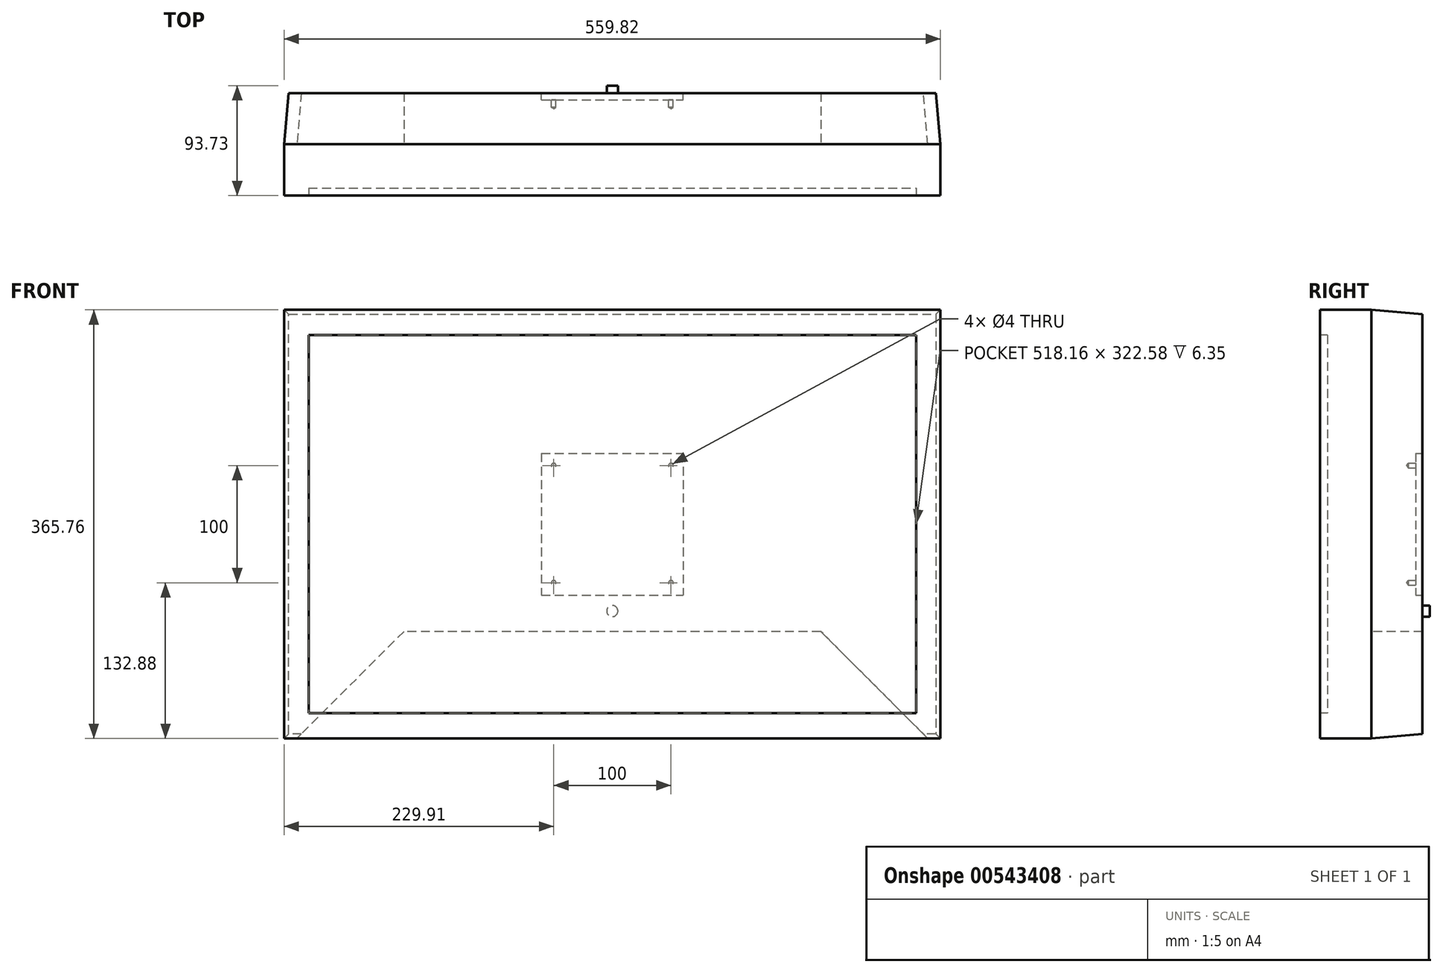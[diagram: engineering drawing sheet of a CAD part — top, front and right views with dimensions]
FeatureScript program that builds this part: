
annotation { "Feature Type Name" : "Feature", "Feature Type Description" : "" }
export const myFeature = defineFeature(function(context is Context, id is Id, definition is map)
    precondition{}
    {
        {
            var Q0;
            Q0=qCreatedBy(makeId("Front.planeOp"),FACE);
            var sketch = newSketch(context, id + "F0", { "sketchPlane" : qUnion([Q0])});
            skLineSegment(sketch, "E0.bottom", {"start": v(-279.9, 182.88) * mm, "end": v(279.9, 182.88) * mm});
            skLineSegment(sketch, "E0.top", {"start": v(-279.9, -182.88) * mm, "end": v(279.9, -182.88) * mm});
            skLineSegment(sketch, "E0.left", {"start": v(-279.9, 182.88) * mm, "end": v(-279.9, -182.88) * mm});
            skLineSegment(sketch, "E0.right", {"start": v(279.9, 182.88) * mm, "end": v(279.9, -182.88) * mm});
            skPoint(sketch, "E0.middle", {"position": v(0, 0) * mm});
            skSolve(sketch);
        }
        {
            var Q0;
            Q0 = qSketchRegion(id + "F0", true);
            extrude(context, id + "F1", {"entities" : qUnion([Q0]), "endBound" : BoundingType.SYMMETRIC, "depth" : 87.38 * mm, "offsetDistance" : 25.4 * mm});
        }
        {
            var Q0;
            Q0=makeQuery(id+"F1.opExtrude","CAP_FACE",FACE,{"disambiguationData":[OSD([sQuery(id+"F0.wireOp",EDGE,"E0.bottom"),sQuery(id+"F0.wireOp",EDGE,"E0.top"),sQuery(id+"F0.wireOp",EDGE,"E0.left"),sQuery(id+"F0.wireOp",EDGE,"E0.right")])],"isStart":false});
            var sketch = newSketch(context, id + "F2", { "sketchPlane" : qUnion([Q0])});
            skLineSegment(sketch, "E1.bottom", {"start": v(-259.08, 161.3) * mm, "end": v(259.08, 161.3) * mm});
            skLineSegment(sketch, "E1.top", {"start": v(-259.08, -161.3) * mm, "end": v(259.08, -161.3) * mm});
            skLineSegment(sketch, "E1.left", {"start": v(-259.08, 161.3) * mm, "end": v(-259.08, -161.3) * mm});
            skLineSegment(sketch, "E1.right", {"start": v(259.08, 161.3) * mm, "end": v(259.08, -161.3) * mm});
            skPoint(sketch, "E1.middle", {"position": v(0, 0) * mm});
            skLineSegment(sketch, "E2", {"start": v(-259.08, -161.3) * mm, "end": v(259.08, 161.3) * mm, "construction": true});
            skSolve(sketch);
        }
        {
            var Q0;
            Q0 = qSketchRegion(id + "F2", true);
            extrude(context, id + "F3", {"entities" : qUnion([Q0]), "operationType" : NewBodyOperationType.REMOVE, "oppositeDirection" : true, "depth" : 6.35 * mm, "offsetDistance" : 25.4 * mm});
        }
        {
            var Q0;
            Q0=makeQuery(id+"F1.opExtrude","CAP_EDGE",EDGE,{"disambiguationData":[OSD([sQuery(id+"F0.wireOp",EDGE,"E0.right")])],"isStart":true});
            var Q1;
            Q1=makeQuery(id+"F1.opExtrude","CAP_EDGE",EDGE,{"disambiguationData":[OSD([sQuery(id+"F0.wireOp",EDGE,"E0.bottom")])],"isStart":true});
            var Q2;
            Q2=makeQuery(id+"F1.opExtrude","CAP_EDGE",EDGE,{"disambiguationData":[OSD([sQuery(id+"F0.wireOp",EDGE,"E0.left")])],"isStart":true});
            var Q3;
            Q3=makeQuery(id+"F1.opExtrude","CAP_EDGE",EDGE,{"disambiguationData":[OSD([sQuery(id+"F0.wireOp",EDGE,"E0.top")])],"isStart":true});
            chamfer(context, id + "F4", {"entities" : qUnion([Q0, Q1, Q2, Q3]), "chamferType" : ChamferType.TWO_OFFSETS, "width1" : ((22.04 - 14.25) / 2) * mm, "oppositeDirection" : false, "width2" : 43.69 * mm, "tangentPropagation" : true});
        }
        {
            var Q0;
            Q0=makeQuery(id+"F1.opExtrude","CAP_FACE",FACE,{"disambiguationData":[OSD([sQuery(id+"F0.wireOp",EDGE,"E0.bottom"),sQuery(id+"F0.wireOp",EDGE,"E0.top"),sQuery(id+"F0.wireOp",EDGE,"E0.left"),sQuery(id+"F0.wireOp",EDGE,"E0.right")])],"isStart":true});
            var sketch = newSketch(context, id + "F5", { "sketchPlane" : qUnion([Q0])});
            skLineSegment(sketch, "E3.bottom", {"start": v(60.45, 60.45) * mm, "end": v(-60.45, 60.45) * mm});
            skLineSegment(sketch, "E3.top", {"start": v(60.45, -60.45) * mm, "end": v(-60.45, -60.45) * mm});
            skLineSegment(sketch, "E3.left", {"start": v(60.45, 60.45) * mm, "end": v(60.45, -60.45) * mm});
            skLineSegment(sketch, "E3.right", {"start": v(-60.45, 60.45) * mm, "end": v(-60.45, -60.45) * mm});
            skPoint(sketch, "E3.middle", {"position": v(0, 0) * mm});
            skSolve(sketch);
        }
        {
            var Q0;
            Q0 = qSketchRegion(id + "F5", true);
            extrude(context, id + "F6", {"entities" : qUnion([Q0]), "operationType" : NewBodyOperationType.REMOVE, "oppositeDirection" : true, "depth" : 5.92 * mm, "offsetDistance" : 25.4 * mm});
        }
        {
            var Q0;
            {var subQ0=sQuery(id+"F0.wireOp",EDGE,"E0.right");var subQ1=sQuery(id+"F0.wireOp",EDGE,"E0.top");Q0=makeQuery(id+"F4.opChamfer","BLEND_VERTEX",VERTEX,{"blendedFrom":[makeQuery(id+"F1.opExtrude","CAP_EDGE",EDGE,{"disambiguationData":[OSD([subQ1])],"isStart":true}),makeQuery(id+"F1.opExtrude","CAP_EDGE",EDGE,{"disambiguationData":[OSD([subQ0])],"isStart":true}),makeQuery(id+"F1.opExtrude","SWEPT_FACE",FACE,{"disambiguationData":[OSD([subQ1])]}),makeQuery(id+"F1.opExtrude","SWEPT_FACE",FACE,{"disambiguationData":[OSD([subQ0])]})],"blendedInto":[makeQuery(id+"F1.opExtrude","SWEPT_FACE",FACE,{"disambiguationData":[OSD([subQ1])]}),makeQuery(id+"F1.opExtrude","SWEPT_FACE",FACE,{"disambiguationData":[OSD([subQ0])]})]});}
            var Q1;
            Q1=makeQuery(id+"F3.boolean.opBoolean","COPY",FACE,{"derivedFrom":makeQuery(id+"F3.opExtrude","CAP_FACE",FACE,{"disambiguationData":[OSD([sQuery(id+"F2.wireOp",EDGE,"E1.bottom"),sQuery(id+"F2.wireOp",EDGE,"E1.top"),sQuery(id+"F2.wireOp",EDGE,"E1.left"),sQuery(id+"F2.wireOp",EDGE,"E1.right")])],"isStart":false})});
            cPlane(context, id + "F7", {"entities" : qUnion([Q0, Q1]), "cplaneType" : CPlaneType.PLANE_POINT, "offset" : 25.4 * mm, "width" : 152.4 * mm, "height" : 152.4 * mm});
        }
        {
            var Q0;
            Q0=qCreatedBy(id+"F7.planeOp",FACE);
            var sketch = newSketch(context, id + "F8", { "sketchPlane" : qUnion([Q0])});
            skLineSegment(sketch, "E4", {"start": v(269.13, -182.88) * mm, "end": v(177.82, -91.57) * mm});
            skLineSegment(sketch, "E5", {"start": v(177.82, -91.57) * mm, "end": v(-177.82, -91.57) * mm});
            skLineSegment(sketch, "E6", {"start": v(-177.82, -91.57) * mm, "end": v(-269.13, -182.88) * mm});
            skLineSegment(sketch, "E7", {"start": v(269.13, -182.88) * mm, "end": v(-269.13, -182.88) * mm});
            skSolve(sketch);
        }
        {
            var Q0;
            Q0 = qSketchRegion(id + "F8", true);
            extrude(context, id + "F9", {"entities" : qUnion([Q0]), "operationType" : NewBodyOperationType.REMOVE, "endBound" : BoundingType.THROUGH_ALL, "oppositeDirection" : true, "depth" : 25.4 * mm, "offsetDistance" : 25.4 * mm});
        }
        {
            var Q0;
            Q0=makeQuery(id+"F6.boolean.opBoolean","COPY",FACE,{"derivedFrom":makeQuery(id+"F6.opExtrude","CAP_FACE",FACE,{"disambiguationData":[OSD([sQuery(id+"F5.wireOp",EDGE,"E3.bottom"),sQuery(id+"F5.wireOp",EDGE,"E3.top"),sQuery(id+"F5.wireOp",EDGE,"E3.left"),sQuery(id+"F5.wireOp",EDGE,"E3.right")])],"isStart":false})});
            var sketch = newSketch(context, id + "F10", { "sketchPlane" : qUnion([Q0])});
            skPoint(sketch, "E8", {"position": v(-50, 50) * mm});
            skPoint(sketch, "E9", {"position": v(50, 50) * mm});
            skPoint(sketch, "E10", {"position": v(50, -50) * mm});
            skPoint(sketch, "E11", {"position": v(-50, -50) * mm});
            skLineSegment(sketch, "E12", {"start": v(0, 74.06) * mm, "end": v(0, -76.48) * mm, "construction": true});
            skPoint(sketch, "E12.endSnap0", {"position": v(0, -60.45) * mm});
            skLineSegment(sketch, "E13", {"start": v(-72.68, 0) * mm, "end": v(74.06, 0) * mm, "construction": true});
            skPoint(sketch, "E13.startSnap0", {"position": v(-60.45, 0) * mm});
            skSolve(sketch);
        }
        {
            var Q0;
            Q0=sQuery(id+"F10.wireOp",VERTEX,"E8");
            var Q1;
            Q1=sQuery(id+"F10.wireOp",VERTEX,"E9");
            var Q2;
            Q2=sQuery(id+"F10.wireOp",VERTEX,"E10");
            var Q3;
            Q3=sQuery(id+"F10.wireOp",VERTEX,"E11");
            var Q4;
            Q4=makeQuery(id+"F1.opExtrude","SWEPT_BODY",BODY,{"disambiguationData":[OSD([sQuery(id+"F0.wireOp",EDGE,"E0.bottom"),sQuery(id+"F0.wireOp",EDGE,"E0.top"),sQuery(id+"F0.wireOp",EDGE,"E0.left"),sQuery(id+"F0.wireOp",EDGE,"E0.right")])]});
            hole(context, id + "F11", {"style" : HoleStyle.SIMPLE, "endStyle" : HoleEndStyle.BLIND, "holeDiameter" : 4 * mm, "majorDiameter" : 6.35 * mm, "holeDepth" : 6.35 * mm, "isTappedThrough" : true, "tappedDepth" : 12.7 * mm, "tapClearance" : 3, "startFromSketch" : true, "locations" : qUnion([Q0, Q1, Q2, Q3]), "scope" : qUnion([Q4])});
        }
        {
            var Q0;
            Q0=makeQuery(id+"F1.opExtrude","CAP_FACE",FACE,{"disambiguationData":[OSD([sQuery(id+"F0.wireOp",EDGE,"E0.bottom"),sQuery(id+"F0.wireOp",EDGE,"E0.top"),sQuery(id+"F0.wireOp",EDGE,"E0.left"),sQuery(id+"F0.wireOp",EDGE,"E0.right")])],"isStart":true});
            var sketch = newSketch(context, id + "F12", { "sketchPlane" : qUnion([Q0])});
            skCircle(sketch, "E14", {"center": v(0, -74.17) * mm, "radius": 4.76 * mm});
            skSolve(sketch);
        }
        {
            var Q0;
            Q0 = qSketchRegion(id + "F12", true);
            extrude(context, id + "F13", {"entities" : qUnion([Q0]), "operationType" : NewBodyOperationType.ADD, "depth" : 6.35 * mm, "offsetDistance" : 25.4 * mm});
        }
    });
